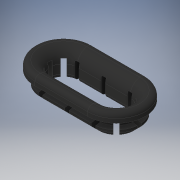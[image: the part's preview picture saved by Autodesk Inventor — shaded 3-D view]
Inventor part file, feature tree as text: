
AUTODESK INVENTOR PART (.ipt)
format: ipt  version: 2019 (Build 230136000, 136)  size: 406,016 bytes
history: native  units: mm
features: extrude x5, projected_geometry x5, sketch x3, fillet x2, mirror x2, thicken_offset x1, chamfer x1
ambient origin geometry x8: Origin, YZ Plane, XZ Plane, XY Plane, X Axis, Y Axis, Z Axis, Center Point
bodies: Solid1 (feature_tree)
feature tree (19):
  sketch  "Sketch1"  dims[d0=6.0mm d1=9.0mm]
  extrude  "Extrusion1"  Depth=9.0mm
  extrude  "Extrusion2"  Depth=2.0mm TaperAngle=0.0deg
  fillet  "Fillet1"  Radius=2.0mm
  thicken_offset  "Thicken1"
  extrude  "Extrusion3"  Depth=3.0mm
  extrude  "Extrusion4"  Depth=10.0mm
  fillet  "Fillet3"  Radius=0.25mm
  chamfer  "Chamfer2"  Distance=2.0mm
  extrude  "Extrusion6"  Depth=10.0mm
  mirror  "Mirror1"
  mirror  "Mirror2"
  sketch  "Sketch2"  dims[d2=1.5mm d3=2.0mm d4=0.0mm d5=2.0mm]
  projected_geometry  "Projected Loop1"
  sketch  "Sketch3"  dims[d6=2.0mm d7=0.0mm d8=3.0mm d9=1.0mm d10=0.25mm d11=0.25mm d12=2.0mm d13=13.962634mm d18=10.0mm d19=10.0mm d20=0.0mm d23=1.25mm d24=1.0mm d25=1.25mm d26=2.0mm d27=45.0deg d32=5.0mm d33=1.0mm d34=30.0mm d36=90.0deg d38=20.0mm d40=6.0mm d41=10.0mm d43=10.0mm d45=10.0mm d46=0.0mm]
  projected_geometry  "Projected Loop2"
  projected_geometry  "Projected Loop3"
  projected_geometry  "Projected Loop4"
  projected_geometry  "Projected Loop5"
